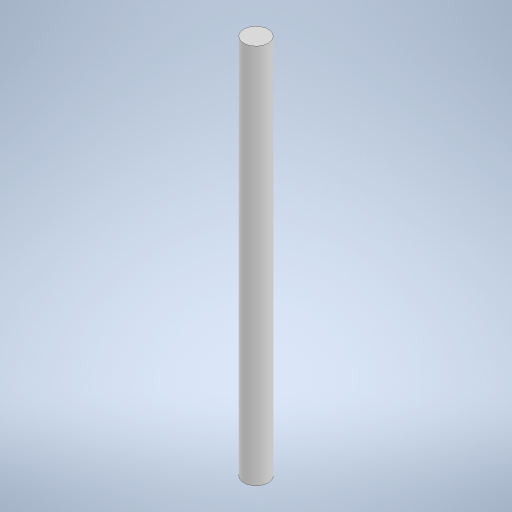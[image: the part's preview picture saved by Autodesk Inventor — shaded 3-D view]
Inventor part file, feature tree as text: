
AUTODESK INVENTOR PART (.ipt)
format: ipt  version: 2023 (Build 270158000, 158)  size: 227,840 bytes
history: native  units: mm
features: extrude x1, sketch x1
ambient origin geometry x8: Origin, YZ Plane, XZ Plane, XY Plane, X Axis, Y Axis, Z Axis, Center Point
bodies: Solid1 (feature_tree)
feature tree (2):
  extrude  "Extrusion1"  Depth=155.5mm TaperAngle=0.0deg
  sketch  "Sketch1"  dims[d0=10.0mm d1=155.5mm d2=0.0mm]
